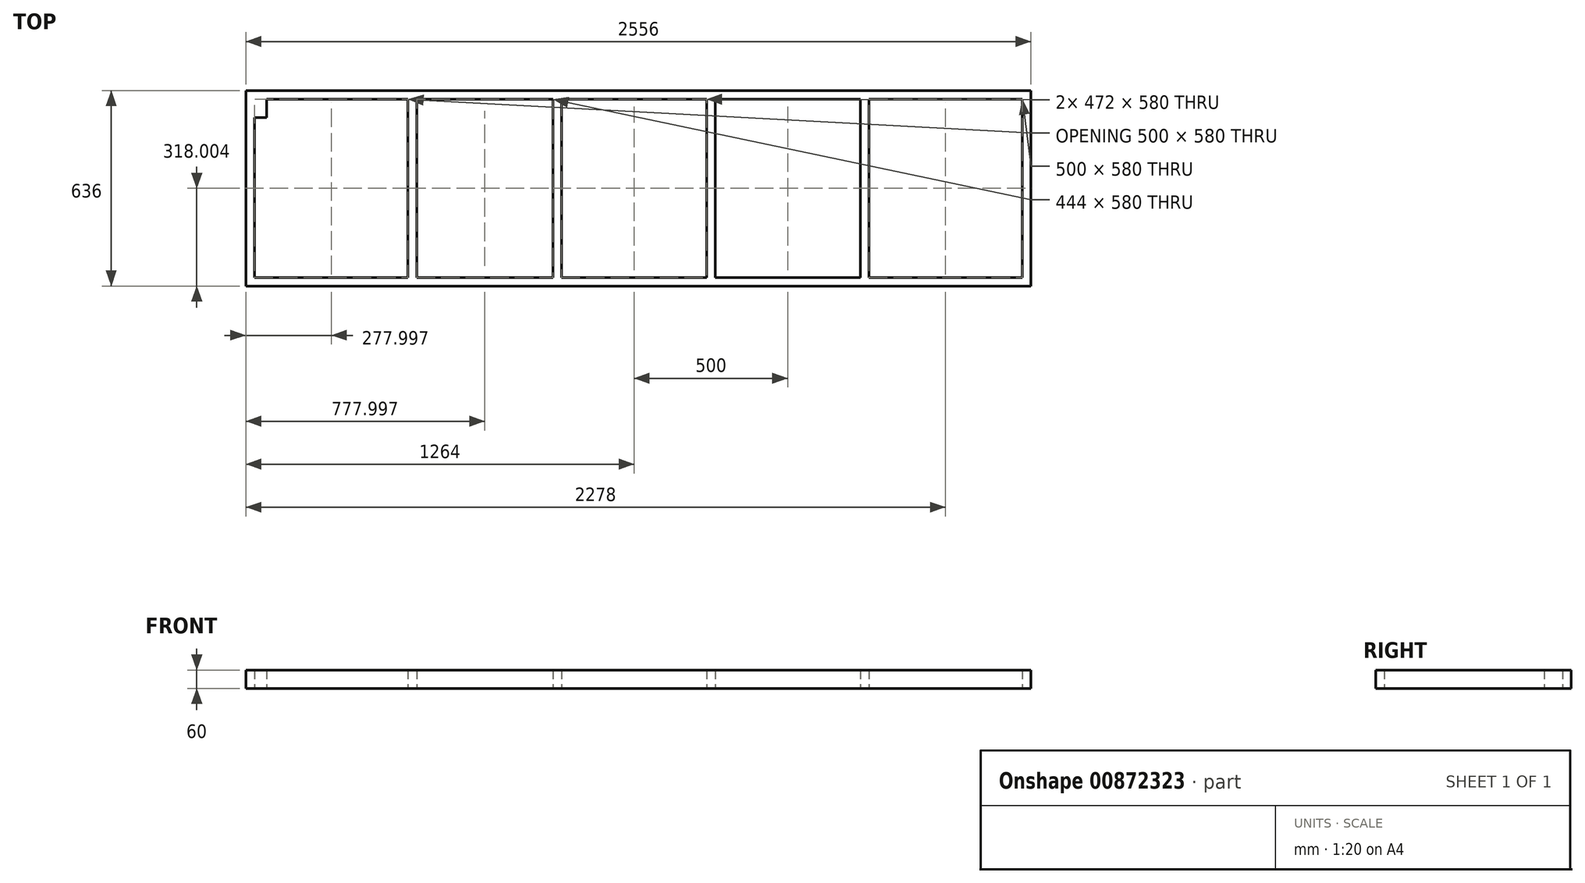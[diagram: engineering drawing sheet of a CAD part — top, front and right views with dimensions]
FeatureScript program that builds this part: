
annotation { "Feature Type Name" : "Feature", "Feature Type Description" : "" }
export const myFeature = defineFeature(function(context is Context, id is Id, definition is map)
    precondition{}
    {
        {
            var Q0;
            Q0=qCreatedBy(makeId("Top.planeOp"),FACE);
            var sketch = newSketch(context, id + "F0", { "sketchPlane" : qUnion([Q0])});
            skLineSegment(sketch, "E0.bottom", {"start": v(-1518.33, 1779.2) * mm, "end": v(2181.67, 1779.2) * mm});
            skLineSegment(sketch, "E0.top", {"start": v(-1518.33, -580.8) * mm, "end": v(2181.67, -580.8) * mm});
            skLineSegment(sketch, "E0.left", {"start": v(-1518.33, 1779.2) * mm, "end": v(-1518.33, -580.8) * mm});
            skLineSegment(sketch, "E0.right", {"start": v(2181.67, 1779.2) * mm, "end": v(2181.67, -580.8) * mm});
            skLineSegment(sketch, "E1.bottom", {"start": v(-268.33, -580.8) * mm, "end": v(-1068.33, -580.8) * mm});
            skLineSegment(sketch, "E1.top", {"start": v(-268.33, -450.05) * mm, "end": v(-1068.33, -450.05) * mm});
            skLineSegment(sketch, "E1.left", {"start": v(-268.33, -580.8) * mm, "end": v(-268.33, -450.05) * mm});
            skLineSegment(sketch, "E1.right", {"start": v(-1068.33, -580.8) * mm, "end": v(-1068.33, -450.05) * mm});
            skLineSegment(sketch, "E2.bottom", {"start": v(-1518.33, -580.8) * mm, "end": v(-918.33, -580.8) * mm});
            skLineSegment(sketch, "E2.left", {"start": v(-1518.33, -580.8) * mm, "end": v(-1518.33, 419.2) * mm});
            skLineSegment(sketch, "E3.bottom", {"start": v(2181.67, -580.8) * mm, "end": v(1181.67, -580.8) * mm});
            skLineSegment(sketch, "E3.left", {"start": v(2181.67, -580.8) * mm, "end": v(2181.67, 19.2) * mm});
            skLineSegment(sketch, "E4.bottom", {"start": v(1181.67, -580.8) * mm, "end": v(181.67, -580.8) * mm});
            skLineSegment(sketch, "E5.bottom", {"start": v(181.67, -580.8) * mm, "end": v(-628.33, -580.8) * mm});
            skLineSegment(sketch, "E6.left", {"start": v(-1518.33, 419.2) * mm, "end": v(-1518.33, 1419.2) * mm});
            skSolve(sketch);
        }
        {
            var Q0;
            Q0=makeQuery(id+"F0.imprint","IMPRINT",FACE,{"disambiguationData":[TD([[makeQuery(id+"F0.imprint","IMPRINT",EDGE,{"derivedFrom":sQuery(id+"F0.wireOp",EDGE,"E0.bottom")}),-1.0]])]});
            var sketch = newSketch(context, id + "F1", { "sketchPlane" : qUnion([Q0])});
            skLineSegment(sketch, "E7.bottom", {"start": v(-1490.33, 1751.2) * mm, "end": v(1009.67, 1751.2) * mm});
            skLineSegment(sketch, "E7.top", {"start": v(-1490.33, 1171.2) * mm, "end": v(1009.67, 1171.2) * mm});
            skLineSegment(sketch, "E7.left", {"start": v(-1490.33, 1751.2) * mm, "end": v(-1490.33, 1171.2) * mm});
            skLineSegment(sketch, "E7.right", {"start": v(1009.67, 1751.2) * mm, "end": v(1009.67, 1171.2) * mm});
            skLineSegment(sketch, "E8.0", {"start": v(-1518.33, 1779.2) * mm, "end": v(1037.67, 1779.2) * mm});
            skLineSegment(sketch, "E8.1", {"start": v(-1518.33, 1779.2) * mm, "end": v(-1518.33, 1143.2) * mm});
            skLineSegment(sketch, "E8.2", {"start": v(-1518.33, 1143.2) * mm, "end": v(1037.67, 1143.2) * mm});
            skLineSegment(sketch, "E8.3", {"start": v(1037.67, 1779.2) * mm, "end": v(1037.67, 1143.2) * mm});
            skLineSegment(sketch, "E9", {"start": v(-990.33, 1751.2) * mm, "end": v(-990.33, 1171.2) * mm});
            skLineSegment(sketch, "E10.0", {"start": v(-962.33, 1751.2) * mm, "end": v(-962.33, 1171.2) * mm});
            skLineSegment(sketch, "E11.1.0.0", {"start": v(-490.33, 1751.2) * mm, "end": v(-490.33, 1171.2) * mm});
            skLineSegment(sketch, "E11.2.0.0", {"start": v(9.67, 1751.2) * mm, "end": v(9.67, 1171.2) * mm});
            skLineSegment(sketch, "E11.3.0.0", {"start": v(509.67, 1751.2) * mm, "end": v(509.67, 1171.2) * mm});
            skLineSegment(sketch, "E11.direction1", {"start": v(-990.33, 1171.2) * mm, "end": v(-490.33, 1171.2) * mm, "construction": true});
            skLineSegment(sketch, "E12.0", {"start": v(481.67, 1751.2) * mm, "end": v(481.67, 1171.2) * mm});
            skLineSegment(sketch, "E13.0", {"start": v(-18.33, 1751.2) * mm, "end": v(-18.33, 1171.2) * mm});
            skLineSegment(sketch, "E14.0", {"start": v(-518.33, 1751.2) * mm, "end": v(-518.33, 1171.2) * mm});
            skSolve(sketch);
        }
        {
            var Q0;
            {var subQ4=sQuery(id+"F1.wireOp",EDGE,"E7.left");Q0=makeQuery(id+"F1.imprint","IMPRINT",FACE,{"disambiguationData":[TD([[makeQuery(id+"F1.imprint","IMPRINT",EDGE,{"derivedFrom":subQ4}),-1.0]])]});}
            var sketch = newSketch(context, id + "F2", { "sketchPlane" : qUnion([Q0])});
            skLineSegment(sketch, "E15.bottom", {"start": v(-1490.33, 1751.2) * mm, "end": v(-1450.33, 1751.2) * mm});
            skLineSegment(sketch, "E15.top", {"start": v(-1490.33, 1691.2) * mm, "end": v(-1450.33, 1691.2) * mm});
            skLineSegment(sketch, "E15.left", {"start": v(-1490.33, 1751.2) * mm, "end": v(-1490.33, 1691.2) * mm});
            skLineSegment(sketch, "E15.right", {"start": v(-1450.33, 1751.2) * mm, "end": v(-1450.33, 1691.2) * mm});
            skSolve(sketch);
        }
        {
            var Q0;
            {var subQ4=sQuery(id+"F1.wireOp",EDGE,"E7.left");Q0=makeQuery(id+"F1.imprint","IMPRINT",FACE,{"disambiguationData":[TD([[makeQuery(id+"F1.imprint","IMPRINT",EDGE,{"derivedFrom":subQ4}),-1.0]])]});}
            var Q1;
            {var subQ0=sQuery(id+"F1.wireOp",EDGE,"E9");Q1=makeQuery(id+"F1.imprint","IMPRINT",FACE,{"disambiguationData":[TD([[makeQuery(id+"F1.imprint","IMPRINT",EDGE,{"derivedFrom":subQ0}),1.0]])]});}
            var Q2;
            {var subQ0=sQuery(id+"F1.wireOp",EDGE,"E11.1.0.0");Q2=makeQuery(id+"F1.imprint","IMPRINT",FACE,{"disambiguationData":[TD([[makeQuery(id+"F1.imprint","IMPRINT",EDGE,{"derivedFrom":subQ0}),-1.0]])]});}
            var Q3;
            {var subQ0=sQuery(id+"F1.wireOp",EDGE,"E11.2.0.0");Q3=makeQuery(id+"F1.imprint","IMPRINT",FACE,{"disambiguationData":[TD([[makeQuery(id+"F1.imprint","IMPRINT",EDGE,{"derivedFrom":subQ0}),-1.0]])]});}
            var Q4;
            {var subQ0=sQuery(id+"F1.wireOp",EDGE,"E11.3.0.0");Q4=makeQuery(id+"F1.imprint","IMPRINT",FACE,{"disambiguationData":[TD([[makeQuery(id+"F1.imprint","IMPRINT",EDGE,{"derivedFrom":subQ0}),-1.0]])]});}
            extrude(context, id + "F3", {"entities" : qUnion([Q0, Q1, Q2, Q3, Q4]), "depth" : 60 * mm, "offsetDistance" : 25 * mm});
        }
        {
            var Q0;
            Q0=makeQuery(id+"F2.imprint","IMPRINT",FACE,{"disambiguationData":[TD([[makeQuery(id+"F2.imprint","IMPRINT",EDGE,{"derivedFrom":sQuery(id+"F2.wireOp",EDGE,"E15.bottom")}),-1.0]])]});
            extrude(context, id + "F4", {"entities" : qUnion([Q0]), "operationType" : NewBodyOperationType.ADD, "depth" : 60 * mm, "offsetDistance" : 25 * mm});
        }
    });
